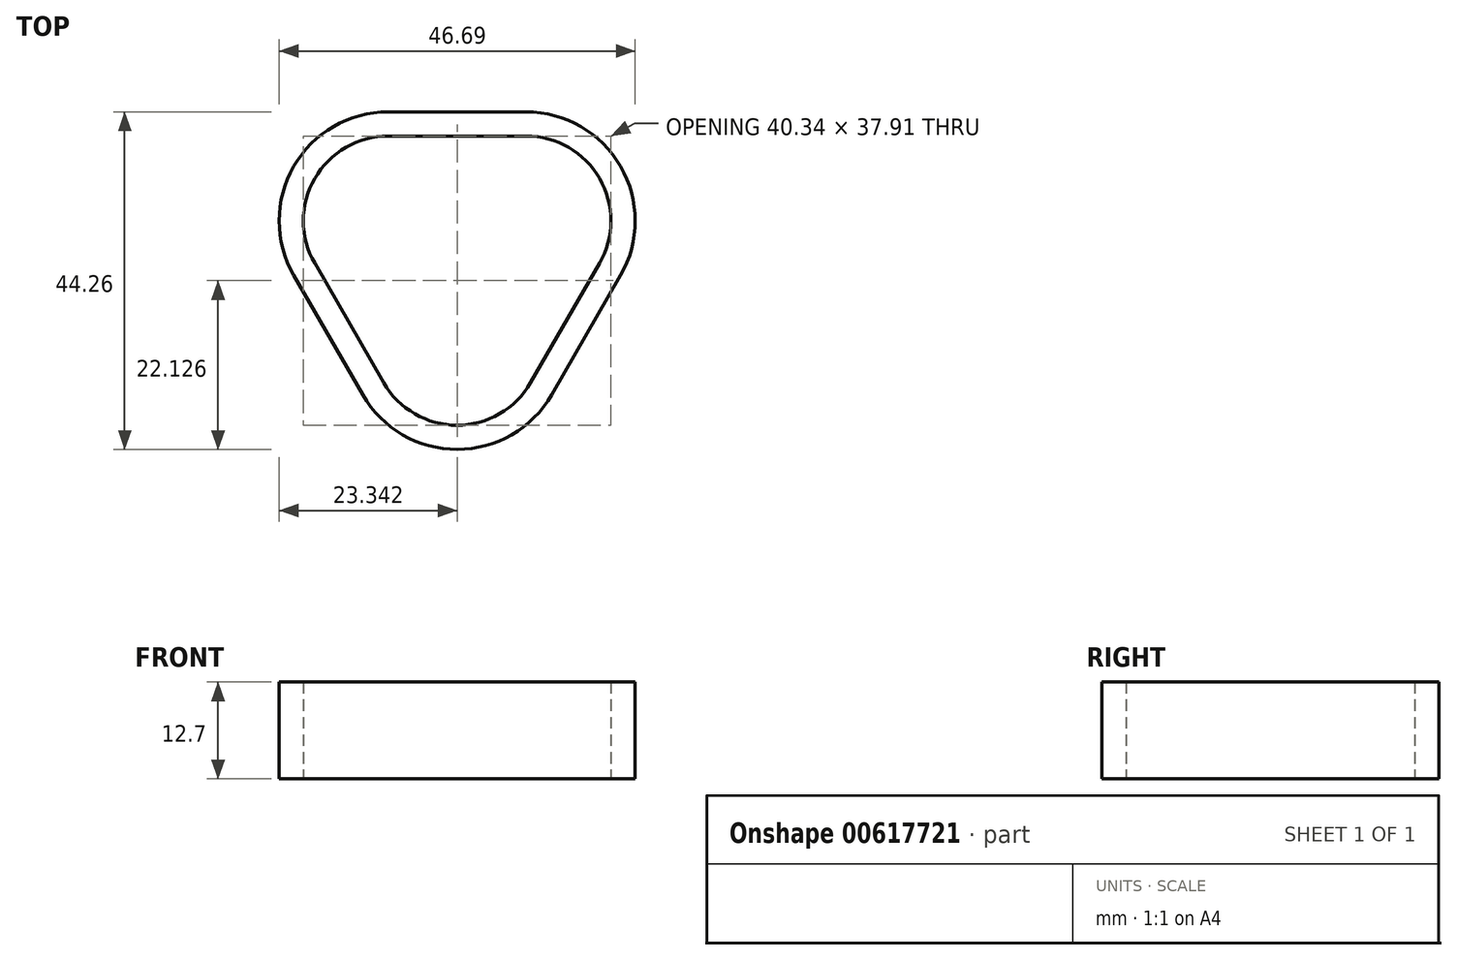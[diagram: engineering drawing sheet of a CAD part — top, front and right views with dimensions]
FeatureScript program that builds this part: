
annotation { "Feature Type Name" : "Feature", "Feature Type Description" : "" }
export const myFeature = defineFeature(function(context is Context, id is Id, definition is map)
    precondition{}
    {
        {
            var Q0;
            Q0=qCreatedBy(makeId("Top.planeOp"),FACE);
            var sketch = newSketch(context, id + "F0", { "sketchPlane" : qUnion([Q0])});
            skArc(sketch, "E0", {"start": v(-26.36, 36.75) * mm, "mid": v(-35.99, 31.2) * mm, "end": v(-35.99, 20.08) * mm});
            skArc(sketch, "E1.trimOffspring", {"start": v(1.37, 20.08) * mm, "mid": v(1.37, 31.2) * mm, "end": v(-8.25, 36.75) * mm});
            skArc(sketch, "E2.trimOffspring", {"start": v(-26.93, 4.4) * mm, "mid": v(-17.3, -1.16) * mm, "end": v(-7.68, 4.4) * mm});
            skLineSegment(sketch, "E3", {"start": v(-26.36, 25.64) * mm, "end": v(-8.25, 25.64) * mm});
            skLineSegment(sketch, "E4", {"start": v(-8.25, 25.64) * mm, "end": v(-17.3, 9.95) * mm});
            skLineSegment(sketch, "E5", {"start": v(-17.3, 9.95) * mm, "end": v(-26.36, 25.64) * mm});
            skLineSegment(sketch, "E6", {"start": v(-26.36, 36.75) * mm, "end": v(-8.25, 36.75) * mm});
            skLineSegment(sketch, "E7", {"start": v(1.37, 20.08) * mm, "end": v(-7.68, 4.4) * mm});
            skLineSegment(sketch, "E8", {"start": v(-35.99, 20.08) * mm, "end": v(-26.93, 4.4) * mm});
            skArc(sketch, "E9.0", {"start": v(-26.36, 39.93) * mm, "mid": v(-38.74, 32.78) * mm, "end": v(-38.74, 18.5) * mm});
            skArc(sketch, "E9.1", {"start": v(4.12, 18.5) * mm, "mid": v(4.12, 32.78) * mm, "end": v(-8.25, 39.93) * mm});
            skLineSegment(sketch, "E9.2", {"start": v(4.12, 18.5) * mm, "end": v(-4.93, 2.81) * mm});
            skLineSegment(sketch, "E9.3", {"start": v(-26.36, 39.93) * mm, "end": v(-8.25, 39.93) * mm});
            skArc(sketch, "E9.4", {"start": v(-29.68, 2.81) * mm, "mid": v(-17.3, -4.33) * mm, "end": v(-4.93, 2.81) * mm});
            skLineSegment(sketch, "E9.5", {"start": v(-38.74, 18.5) * mm, "end": v(-29.68, 2.81) * mm});
            skSolve(sketch);
        }
        {
            var Q0;
            Q0=makeQuery(id+"F0.imprint","IMPRINT",FACE,{"disambiguationData":[TD([[makeQuery(id+"F0.imprint","IMPRINT",EDGE,{"derivedFrom":sQuery(id+"F0.wireOp",EDGE,"E0")}),-1.0]])]});
            extrude(context, id + "F1", {"entities" : qUnion([Q0]), "depth" : 12.7 * mm, "offsetDistance" : 25.4 * mm});
        }
    });
